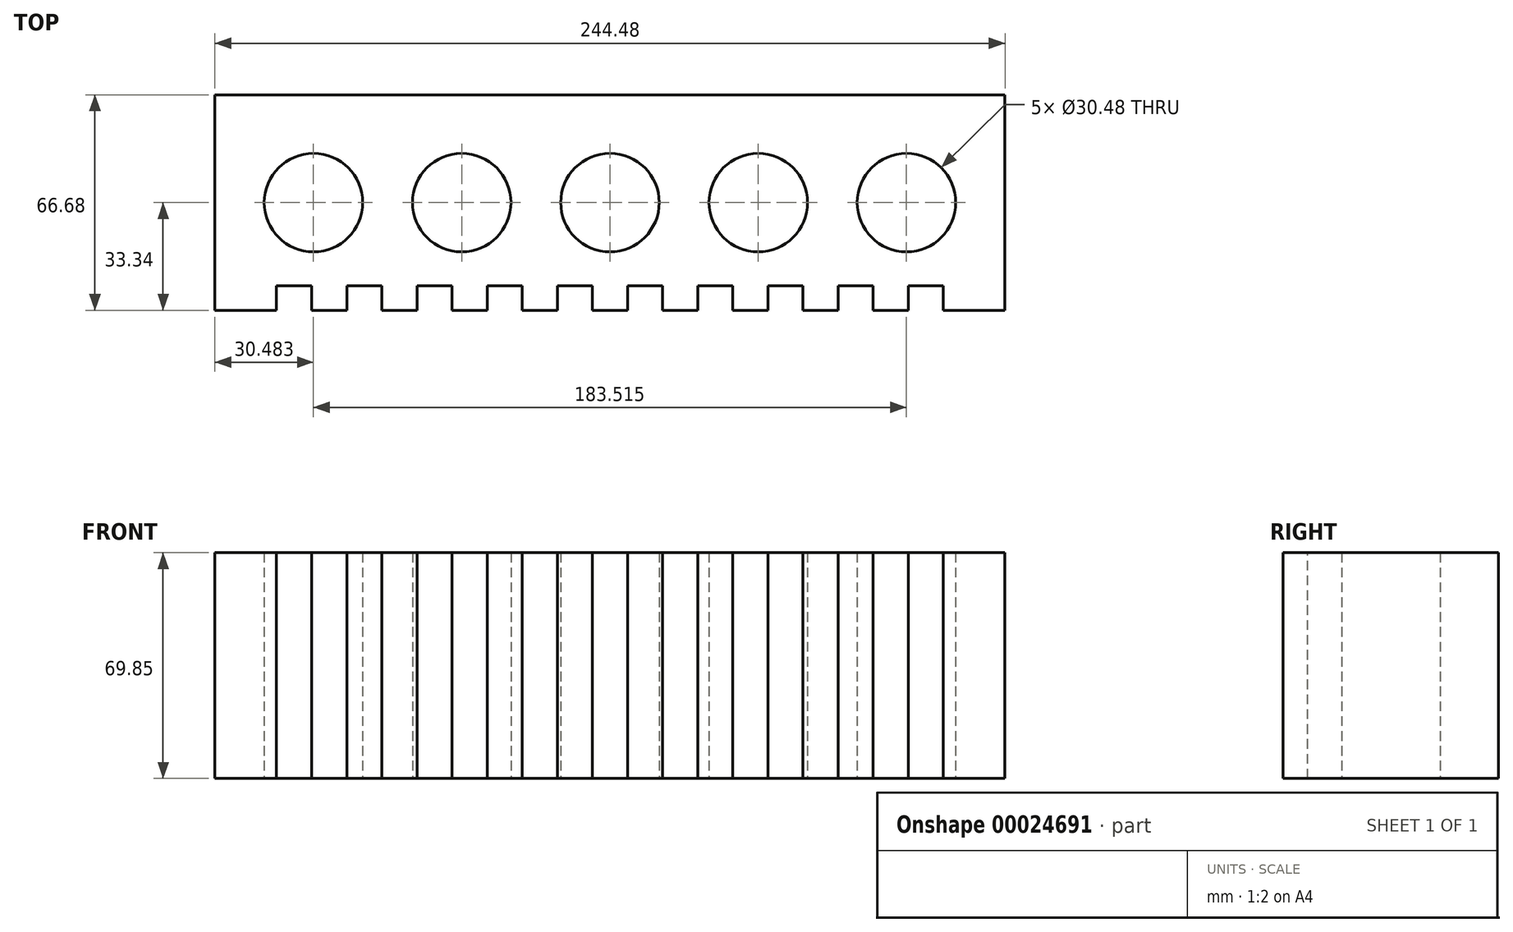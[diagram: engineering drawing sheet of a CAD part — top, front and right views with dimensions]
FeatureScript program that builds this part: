
annotation { "Feature Type Name" : "Feature", "Feature Type Description" : "" }
export const myFeature = defineFeature(function(context is Context, id is Id, definition is map)
    precondition{}
    {
        {
            var Q0;
            Q0=qCreatedBy(makeId("Top.planeOp"),FACE);
            var sketch = newSketch(context, id + "F0", { "sketchPlane" : qUnion([Q0])});
            skLineSegment(sketch, "E0.bottom", {"start": v(-122.24, -33.34) * mm, "end": v(122.24, -33.34) * mm});
            skLineSegment(sketch, "E0.top", {"start": v(-122.24, 33.34) * mm, "end": v(122.24, 33.34) * mm});
            skLineSegment(sketch, "E0.left", {"start": v(-122.24, -33.34) * mm, "end": v(-122.24, 33.34) * mm});
            skLineSegment(sketch, "E0.right", {"start": v(122.24, -33.34) * mm, "end": v(122.24, 33.34) * mm});
            skCircle(sketch, "E1", {"center": v(-91.76, 0) * mm, "radius": 15.24 * mm});
            skCircle(sketch, "E2", {"center": v(-45.88, 0) * mm, "radius": 15.24 * mm});
            skCircle(sketch, "E3", {"center": v(0, 0) * mm, "radius": 15.24 * mm});
            skCircle(sketch, "E4", {"center": v(45.88, 0) * mm, "radius": 15.24 * mm});
            skCircle(sketch, "E5", {"center": v(91.76, 0) * mm, "radius": 15.24 * mm});
            skLineSegment(sketch, "E6", {"start": v(-91.76, 0) * mm, "end": v(-45.88, 0) * mm, "construction": true});
            skLineSegment(sketch, "E7", {"start": v(0, 0) * mm, "end": v(-45.88, 0) * mm, "construction": true});
            skLineSegment(sketch, "E8", {"start": v(0, 0) * mm, "end": v(45.88, 0) * mm, "construction": true});
            skLineSegment(sketch, "E9", {"start": v(45.88, 0) * mm, "end": v(91.76, 0) * mm, "construction": true});
            skLineSegment(sketch, "E10", {"start": v(-91.76, 0) * mm, "end": v(-122.24, 0) * mm, "construction": true});
            skLineSegment(sketch, "E11", {"start": v(91.76, 0) * mm, "end": v(122.24, 0) * mm, "construction": true});
            skSolve(sketch);
        }
        {
            var Q0;
            Q0=makeQuery(id+"F0.imprint","IMPRINT",FACE,{"disambiguationData":[TD([[makeQuery(id+"F0.imprint","IMPRINT",EDGE,{"derivedFrom":sQuery(id+"F0.wireOp",EDGE,"E0.bottom")}),1.0]])]});
            extrude(context, id + "F1", {"entities" : qUnion([Q0]), "depth" : 69.85 * mm});
        }
        {
            var Q0;
            Q0=makeQuery(id+"F1.opExtrude","CAP_FACE",FACE,{"disambiguationData":[OSD([sQuery(id+"F0.wireOp",EDGE,"E0.bottom"),sQuery(id+"F0.wireOp",EDGE,"E0.top"),sQuery(id+"F0.wireOp",EDGE,"E0.left"),sQuery(id+"F0.wireOp",EDGE,"E0.right"),sQuery(id+"F0.wireOp",EDGE,"E1"),sQuery(id+"F0.wireOp",EDGE,"E2"),sQuery(id+"F0.wireOp",EDGE,"E3"),sQuery(id+"F0.wireOp",EDGE,"E4"),sQuery(id+"F0.wireOp",EDGE,"E5")])],"isStart":false});
            var sketch = newSketch(context, id + "F2", { "sketchPlane" : qUnion([Q0])});
            skLineSegment(sketch, "E12.bottom", {"start": v(-103.19, -33.34) * mm, "end": v(-92.33, -33.34) * mm});
            skLineSegment(sketch, "E12.top", {"start": v(-103.19, -25.72) * mm, "end": v(-92.33, -25.72) * mm});
            skLineSegment(sketch, "E12.left", {"start": v(-103.19, -33.34) * mm, "end": v(-103.19, -25.72) * mm});
            skLineSegment(sketch, "E12.right", {"start": v(-92.33, -33.34) * mm, "end": v(-92.33, -25.72) * mm});
            skLineSegment(sketch, "E13", {"start": v(-103.19, -25.72) * mm, "end": v(-122.24, -25.72) * mm, "construction": true});
            skLineSegment(sketch, "E14.1.0.0", {"start": v(-70.6, -33.34) * mm, "end": v(-70.6, -25.72) * mm});
            skLineSegment(sketch, "E14.1.0.1", {"start": v(-81.46, -25.72) * mm, "end": v(-70.6, -25.72) * mm});
            skLineSegment(sketch, "E14.1.0.2", {"start": v(-81.46, -33.34) * mm, "end": v(-81.46, -25.72) * mm});
            skLineSegment(sketch, "E14.1.0.3", {"start": v(-81.46, -33.34) * mm, "end": v(-70.6, -33.34) * mm});
            skLineSegment(sketch, "E14.2.0.0", {"start": v(-48.88, -33.34) * mm, "end": v(-48.88, -25.72) * mm});
            skLineSegment(sketch, "E14.2.0.1", {"start": v(-59.74, -25.72) * mm, "end": v(-48.88, -25.72) * mm});
            skLineSegment(sketch, "E14.2.0.2", {"start": v(-59.74, -33.34) * mm, "end": v(-59.74, -25.72) * mm});
            skLineSegment(sketch, "E14.2.0.3", {"start": v(-59.74, -33.34) * mm, "end": v(-48.88, -33.34) * mm});
            skLineSegment(sketch, "E14.3.0.0", {"start": v(-27.15, -33.34) * mm, "end": v(-27.15, -25.72) * mm});
            skLineSegment(sketch, "E14.3.0.1", {"start": v(-38.02, -25.72) * mm, "end": v(-27.15, -25.72) * mm});
            skLineSegment(sketch, "E14.3.0.2", {"start": v(-38.02, -33.34) * mm, "end": v(-38.02, -25.72) * mm});
            skLineSegment(sketch, "E14.3.0.3", {"start": v(-38.02, -33.34) * mm, "end": v(-27.15, -33.34) * mm});
            skLineSegment(sketch, "E14.4.0.0", {"start": v(-5.43, -33.34) * mm, "end": v(-5.43, -25.72) * mm});
            skLineSegment(sketch, "E14.4.0.1", {"start": v(-16.3, -25.72) * mm, "end": v(-5.43, -25.72) * mm});
            skLineSegment(sketch, "E14.4.0.2", {"start": v(-16.3, -33.34) * mm, "end": v(-16.3, -25.72) * mm});
            skLineSegment(sketch, "E14.4.0.3", {"start": v(-16.3, -33.34) * mm, "end": v(-5.43, -33.34) * mm});
            skLineSegment(sketch, "E14.5.0.0", {"start": v(16.3, -33.34) * mm, "end": v(16.3, -25.72) * mm});
            skLineSegment(sketch, "E14.5.0.1", {"start": v(5.43, -25.72) * mm, "end": v(16.3, -25.72) * mm});
            skLineSegment(sketch, "E14.5.0.2", {"start": v(5.43, -33.34) * mm, "end": v(5.43, -25.72) * mm});
            skLineSegment(sketch, "E14.5.0.3", {"start": v(5.43, -33.34) * mm, "end": v(16.3, -33.34) * mm});
            skLineSegment(sketch, "E14.6.0.0", {"start": v(38.02, -33.34) * mm, "end": v(38.02, -25.72) * mm});
            skLineSegment(sketch, "E14.6.0.1", {"start": v(27.15, -25.72) * mm, "end": v(38.02, -25.72) * mm});
            skLineSegment(sketch, "E14.6.0.2", {"start": v(27.15, -33.34) * mm, "end": v(27.15, -25.72) * mm});
            skLineSegment(sketch, "E14.6.0.3", {"start": v(27.15, -33.34) * mm, "end": v(38.02, -33.34) * mm});
            skLineSegment(sketch, "E14.7.0.0", {"start": v(59.74, -33.34) * mm, "end": v(59.74, -25.72) * mm});
            skLineSegment(sketch, "E14.7.0.1", {"start": v(48.88, -25.72) * mm, "end": v(59.74, -25.72) * mm});
            skLineSegment(sketch, "E14.7.0.2", {"start": v(48.88, -33.34) * mm, "end": v(48.88, -25.72) * mm});
            skLineSegment(sketch, "E14.7.0.3", {"start": v(48.88, -33.34) * mm, "end": v(59.74, -33.34) * mm});
            skLineSegment(sketch, "E14.8.0.0", {"start": v(81.46, -33.34) * mm, "end": v(81.46, -25.72) * mm});
            skLineSegment(sketch, "E14.8.0.1", {"start": v(70.6, -25.72) * mm, "end": v(81.46, -25.72) * mm});
            skLineSegment(sketch, "E14.8.0.2", {"start": v(70.6, -33.34) * mm, "end": v(70.6, -25.72) * mm});
            skLineSegment(sketch, "E14.8.0.3", {"start": v(70.6, -33.34) * mm, "end": v(81.46, -33.34) * mm});
            skLineSegment(sketch, "E14.9.0.0", {"start": v(103.19, -33.34) * mm, "end": v(103.19, -25.72) * mm});
            skLineSegment(sketch, "E14.9.0.1", {"start": v(92.33, -25.72) * mm, "end": v(103.19, -25.72) * mm});
            skLineSegment(sketch, "E14.9.0.2", {"start": v(92.33, -33.34) * mm, "end": v(92.33, -25.72) * mm});
            skLineSegment(sketch, "E14.9.0.3", {"start": v(92.33, -33.34) * mm, "end": v(103.19, -33.34) * mm});
            skLineSegment(sketch, "E14.direction1", {"start": v(-92.33, -33.34) * mm, "end": v(-70.6, -33.34) * mm, "construction": true});
            skLineSegment(sketch, "E15", {"start": v(103.19, -25.72) * mm, "end": v(122.24, -25.72) * mm, "construction": true});
            skLineSegment(sketch, "E16", {"start": v(-92.33, -25.72) * mm, "end": v(-81.46, -25.72) * mm, "construction": true});
            skSolve(sketch);
        }
        {
            var Q0;
            Q0=makeQuery(id+"F2.imprint","IMPRINT",FACE,{"disambiguationData":[TD([[makeQuery(id+"F2.imprint","IMPRINT",EDGE,{"derivedFrom":sQuery(id+"F2.wireOp",EDGE,"E12.bottom")}),1.0]])]});
            var Q1;
            Q1=makeQuery(id+"F2.imprint","IMPRINT",FACE,{"disambiguationData":[TD([[makeQuery(id+"F2.imprint","IMPRINT",EDGE,{"derivedFrom":sQuery(id+"F2.wireOp",EDGE,"E14.1.0.0")}),1.0]])]});
            var Q2;
            Q2=makeQuery(id+"F2.imprint","IMPRINT",FACE,{"disambiguationData":[TD([[makeQuery(id+"F2.imprint","IMPRINT",EDGE,{"derivedFrom":sQuery(id+"F2.wireOp",EDGE,"E14.2.0.0")}),1.0]])]});
            var Q3;
            Q3=makeQuery(id+"F2.imprint","IMPRINT",FACE,{"disambiguationData":[TD([[makeQuery(id+"F2.imprint","IMPRINT",EDGE,{"derivedFrom":sQuery(id+"F2.wireOp",EDGE,"E14.3.0.0")}),1.0]])]});
            var Q4;
            Q4=makeQuery(id+"F2.imprint","IMPRINT",FACE,{"disambiguationData":[TD([[makeQuery(id+"F2.imprint","IMPRINT",EDGE,{"derivedFrom":sQuery(id+"F2.wireOp",EDGE,"E14.4.0.0")}),1.0]])]});
            var Q5;
            Q5=makeQuery(id+"F2.imprint","IMPRINT",FACE,{"disambiguationData":[TD([[makeQuery(id+"F2.imprint","IMPRINT",EDGE,{"derivedFrom":sQuery(id+"F2.wireOp",EDGE,"E14.5.0.0")}),1.0]])]});
            var Q6;
            Q6=makeQuery(id+"F2.imprint","IMPRINT",FACE,{"disambiguationData":[TD([[makeQuery(id+"F2.imprint","IMPRINT",EDGE,{"derivedFrom":sQuery(id+"F2.wireOp",EDGE,"E14.6.0.0")}),1.0]])]});
            var Q7;
            Q7=makeQuery(id+"F2.imprint","IMPRINT",FACE,{"disambiguationData":[TD([[makeQuery(id+"F2.imprint","IMPRINT",EDGE,{"derivedFrom":sQuery(id+"F2.wireOp",EDGE,"E14.7.0.0")}),1.0]])]});
            var Q8;
            Q8=makeQuery(id+"F2.imprint","IMPRINT",FACE,{"disambiguationData":[TD([[makeQuery(id+"F2.imprint","IMPRINT",EDGE,{"derivedFrom":sQuery(id+"F2.wireOp",EDGE,"E14.8.0.0")}),1.0]])]});
            var Q9;
            Q9=makeQuery(id+"F2.imprint","IMPRINT",FACE,{"disambiguationData":[TD([[makeQuery(id+"F2.imprint","IMPRINT",EDGE,{"derivedFrom":sQuery(id+"F2.wireOp",EDGE,"E14.9.0.0")}),1.0]])]});
            extrude(context, id + "F3", {"entities" : qUnion([Q0, Q1, Q2, Q3, Q4, Q5, Q6, Q7, Q8, Q9]), "operationType" : NewBodyOperationType.REMOVE, "endBound" : BoundingType.THROUGH_ALL, "oppositeDirection" : true, "depth" : 25.4 * mm});
        }
    });
